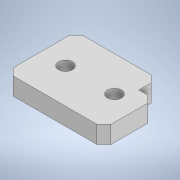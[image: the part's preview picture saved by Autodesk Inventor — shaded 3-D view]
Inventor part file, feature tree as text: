
AUTODESK INVENTOR PART (.ipt)
format: ipt  version: 2022 (Build 260153000, 153)  size: 120,832 bytes
history: native  units: in
note: dims shown in document units (in); Inventor stores cm internally (conversion verified against a paired STEP export)
features: sketch x4, extrude x3, chamfer x1
ambient origin geometry x8: Origin, YZ Plane, XZ Plane, XY Plane, X Axis, Y Axis, Z Axis, Center Point
bodies: Solid1 (feature_tree)
feature tree (8):
  sketch  "Sketch1"  dims[d0=1.1024in d1=0.7874in]
  extrude  "Extrusion1"  Depth=0.7874in
  extrude  "Extrusion2"  Depth=0.1969in
  extrude  "Extrusion3"  Depth=0.2362in TaperAngle=0.0deg
  chamfer  "Chamfer1"  Distance=0.2362in
  sketch  "Sketch2"  dims[d2=0.1969in d3=0.0in d4=0.1575in]
  sketch  "Sketch3"  dims[d5=0.1575in d6=0.2362in d7=0.0in d8=0.2362in d9=0.0in]
  sketch  "Sketch4"  dims[d10=0.0787in d11=0.0787in d12=45.0deg]
